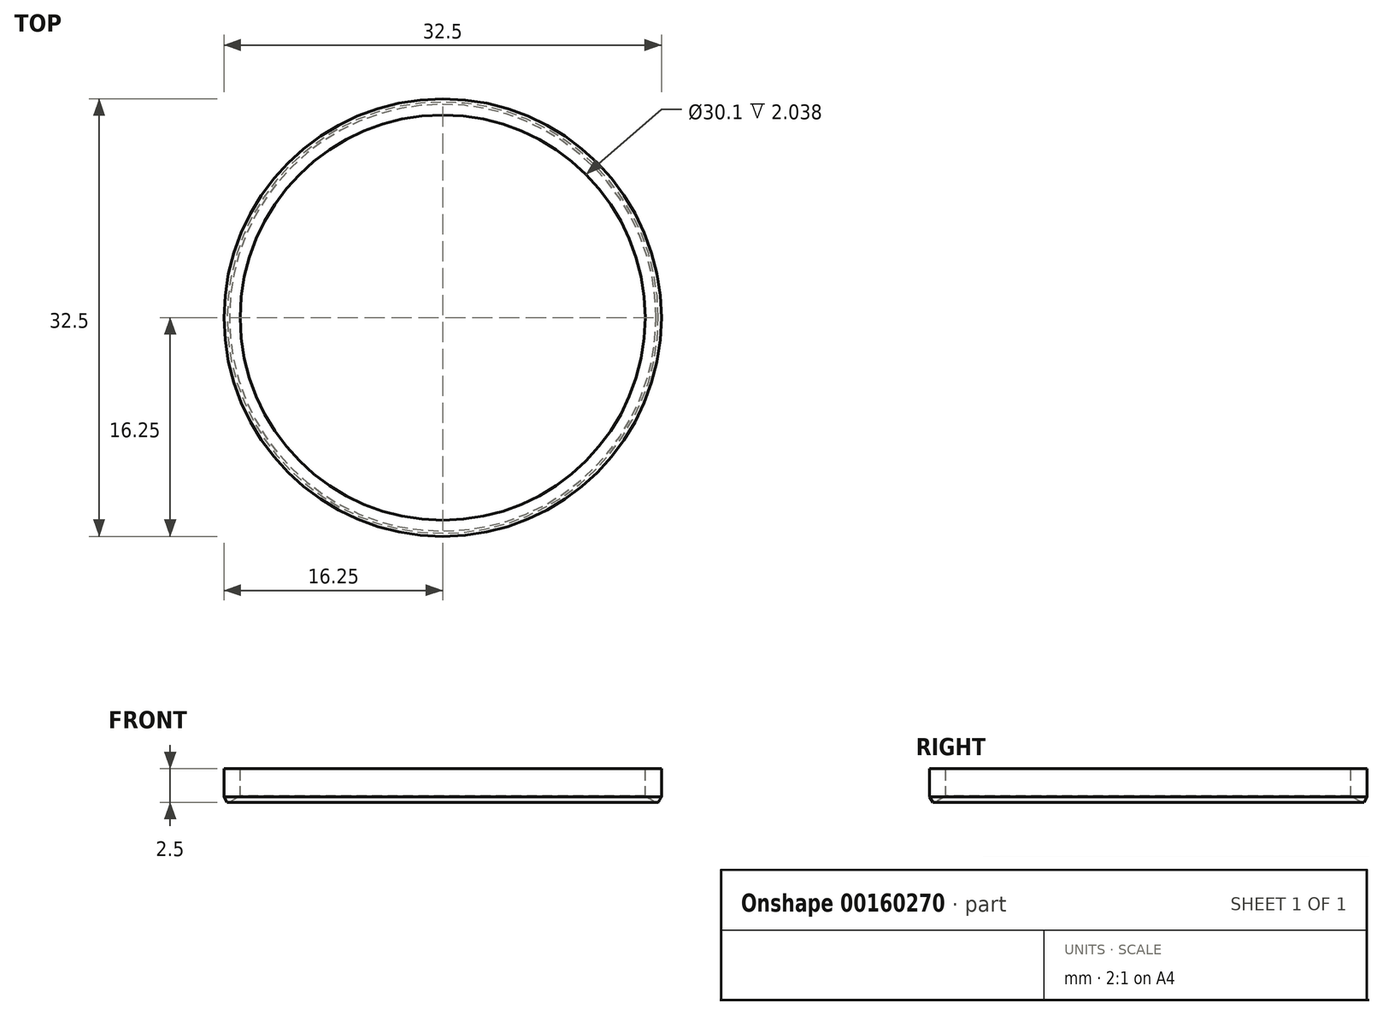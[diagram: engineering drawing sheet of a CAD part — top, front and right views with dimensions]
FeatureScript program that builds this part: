
annotation { "Feature Type Name" : "Feature", "Feature Type Description" : "" }
export const myFeature = defineFeature(function(context is Context, id is Id, definition is map)
    precondition{}
    {
        {
            var Q0;
            Q0=qCreatedBy(makeId("Top.planeOp"),FACE);
            var sketch = newSketch(context, id + "F0", { "sketchPlane" : qUnion([Q0])});
            skCircle(sketch, "E0", {"center": v(0, 0) * mm, "radius": 16.25 * mm});
            skSolve(sketch);
        }
        {
            var Q0;
            Q0=qSketchRegion(id+"F0",true);
            extrude(context, id + "F1", {"entities" : qUnion([Q0]), "depth" : 2.5 * mm});
        }
        {
            var Q0;
            Q0=makeQuery(id+"F1.opExtrude","CAP_FACE",FACE,{"disambiguationData":[OSD([sQuery(id+"F0.wireOp",EDGE,"E0")])],"isStart":false});
            var sketch = newSketch(context, id + "F2", { "sketchPlane" : qUnion([Q0])});
            skCircle(sketch, "E1", {"center": v(0, 0) * mm, "radius": 15.05 * mm});
            skSolve(sketch);
        }
        {
            var Q0;
            Q0=qSketchRegion(id+"F2",true);
            extrude(context, id + "F3", {"entities" : qUnion([Q0]), "operationType" : NewBodyOperationType.REMOVE, "endBound" : BoundingType.THROUGH_ALL, "oppositeDirection" : true, "depth" : 25 * mm});
        }
        {
            var Q0;
            Q0=makeQuery(id+"F3.boolean.opBoolean","COPY",EDGE,{"derivedFrom":makeQuery(id+"F3.opExtrude","CAP_EDGE",EDGE,{"disambiguationData":[OSD([sQuery(id+"F2.wireOp",EDGE,"E1")])],"isStart":true})});
            var Q1;
            Q1=makeQuery(id+"F3.boolean.opBoolean","INTERSECT",EDGE,{"derivedFrom":[makeQuery(id+"F1.opExtrude","CAP_FACE",FACE,{"disambiguationData":[OSD([sQuery(id+"F0.wireOp",EDGE,"E0")])],"isStart":true}),makeQuery(id+"F3.opExtrude","SWEPT_FACE",FACE,{"disambiguationData":[OSD([sQuery(id+"F2.wireOp",EDGE,"E1")])]})]});
            chamfer(context, id + "F4", {"entities" : qUnion([Q0, Q1]), "chamferType" : ChamferType.OFFSET_ANGLE, "width" : 0.8 * mm, "oppositeDirection" : false, "angle" : 30 * degree, "tangentPropagation" : true});
        }
        {
            var Q0;
            Q0=makeQuery(id+"F1.opExtrude","CAP_EDGE",EDGE,{"disambiguationData":[OSD([sQuery(id+"F0.wireOp",EDGE,"E0")])],"isStart":true});
            chamfer(context, id + "F5", {"entities" : qUnion([Q0]), "chamferType" : ChamferType.OFFSET_ANGLE, "width" : 0.4 * mm, "oppositeDirection" : false, "angle" : 30 * degree, "tangentPropagation" : true});
        }
    });
